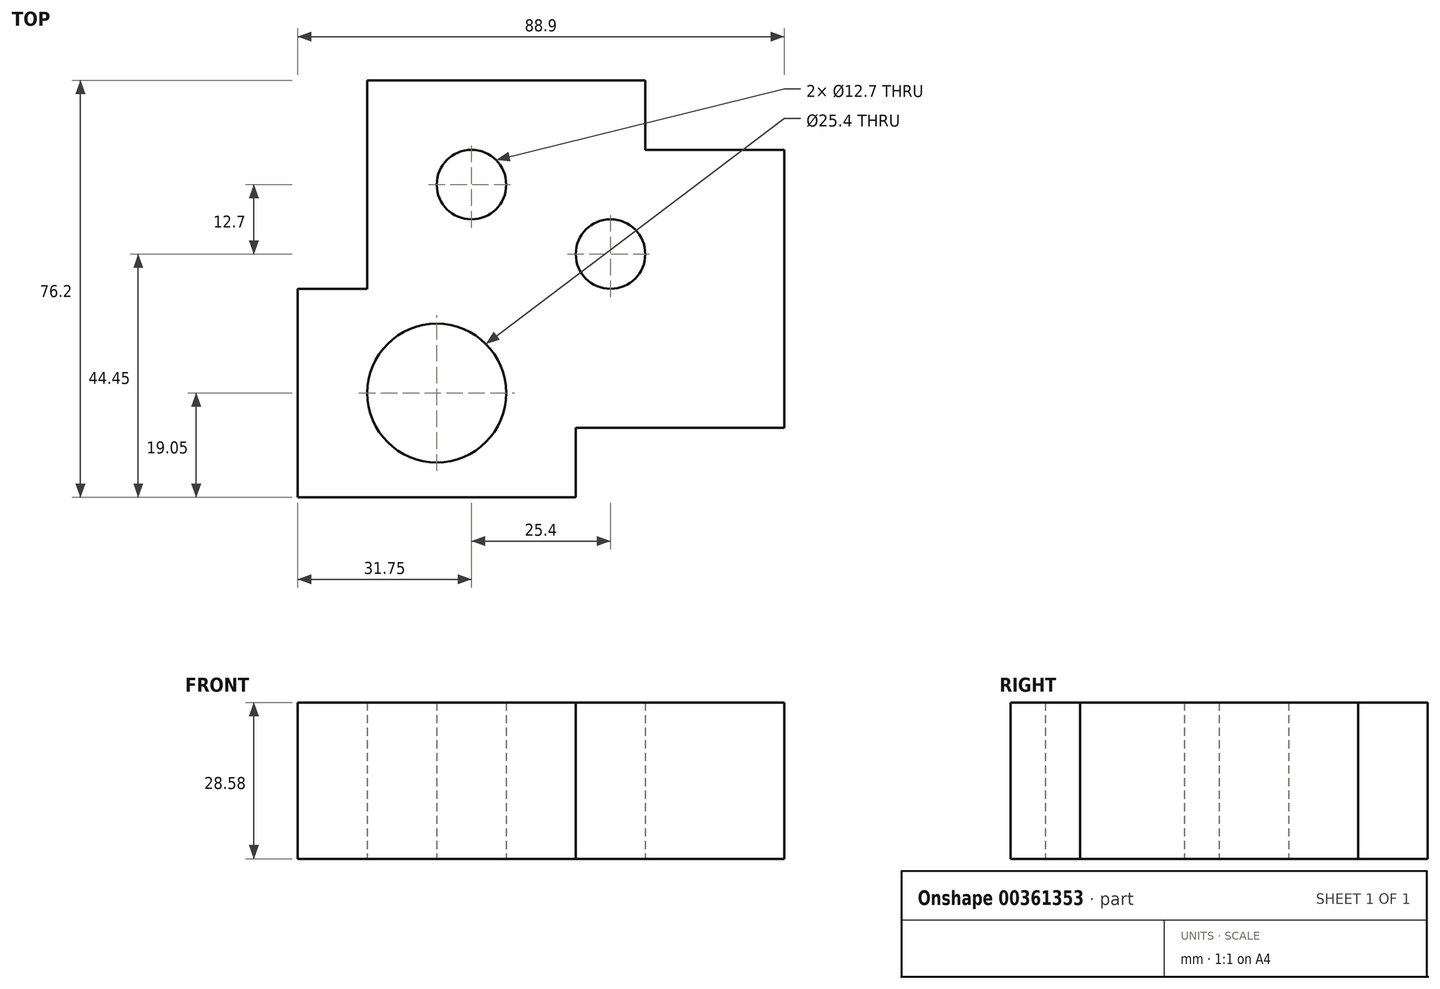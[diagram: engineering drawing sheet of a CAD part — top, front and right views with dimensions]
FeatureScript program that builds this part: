
annotation { "Feature Type Name" : "Feature", "Feature Type Description" : "" }
export const myFeature = defineFeature(function(context is Context, id is Id, definition is map)
    precondition{}
    {
        {
            var Q0;
            Q0=qCreatedBy(makeId("Top.planeOp"),FACE);
            var sketch = newSketch(context, id + "F0", { "sketchPlane" : qUnion([Q0])});
            skLineSegment(sketch, "E0.bottom", {"start": v(6.35, -38.1) * mm, "end": v(-44.45, -38.1) * mm});
            skLineSegment(sketch, "E0.top", {"start": v(19.05, 38.1) * mm, "end": v(-31.75, 38.1) * mm});
            skLineSegment(sketch, "E0.left", {"start": v(44.45, -25.4) * mm, "end": v(44.45, 25.4) * mm});
            skLineSegment(sketch, "E0.right", {"start": v(-44.45, -38.1) * mm, "end": v(-44.45, 0) * mm});
            skPoint(sketch, "E0.middle", {"position": v(0, 0) * mm});
            skLineSegment(sketch, "E1", {"start": v(6.35, -25.4) * mm, "end": v(6.35, -38.1) * mm});
            skLineSegment(sketch, "E2", {"start": v(6.35, -25.4) * mm, "end": v(44.45, -25.4) * mm});
            skPoint(sketch, "E3.orphan", {"position": v(44.45, -38.1) * mm});
            skLineSegment(sketch, "E4", {"start": v(-31.75, 0) * mm, "end": v(-31.75, 38.1) * mm});
            skLineSegment(sketch, "E5", {"start": v(-44.45, 0) * mm, "end": v(-31.75, 0) * mm});
            skPoint(sketch, "E6.orphan", {"position": v(-44.45, 38.1) * mm});
            skLineSegment(sketch, "E7", {"start": v(19.05, 38.1) * mm, "end": v(19.05, 25.4) * mm});
            skLineSegment(sketch, "E8", {"start": v(19.05, 25.4) * mm, "end": v(44.45, 25.4) * mm});
            skPoint(sketch, "E9.orphan", {"position": v(44.45, 38.1) * mm});
            skCircle(sketch, "E10", {"center": v(-19.05, -19.05) * mm, "radius": 12.7 * mm});
            skCircle(sketch, "E11", {"center": v(-12.7, 19.05) * mm, "radius": 6.35 * mm});
            skCircle(sketch, "E12", {"center": v(12.7, 6.35) * mm, "radius": 6.35 * mm});
            skSolve(sketch);
        }
        {
            var Q0;
            Q0=makeQuery(id+"F0.imprint","IMPRINT",FACE,{"disambiguationData":[TD([[makeQuery(id+"F0.imprint","IMPRINT",EDGE,{"derivedFrom":sQuery(id+"F0.wireOp",EDGE,"E0.bottom")}),-1.0]])]});
            extrude(context, id + "F1", {"entities" : qUnion([Q0]), "depth" : 28.57 * mm});
        }
    });
